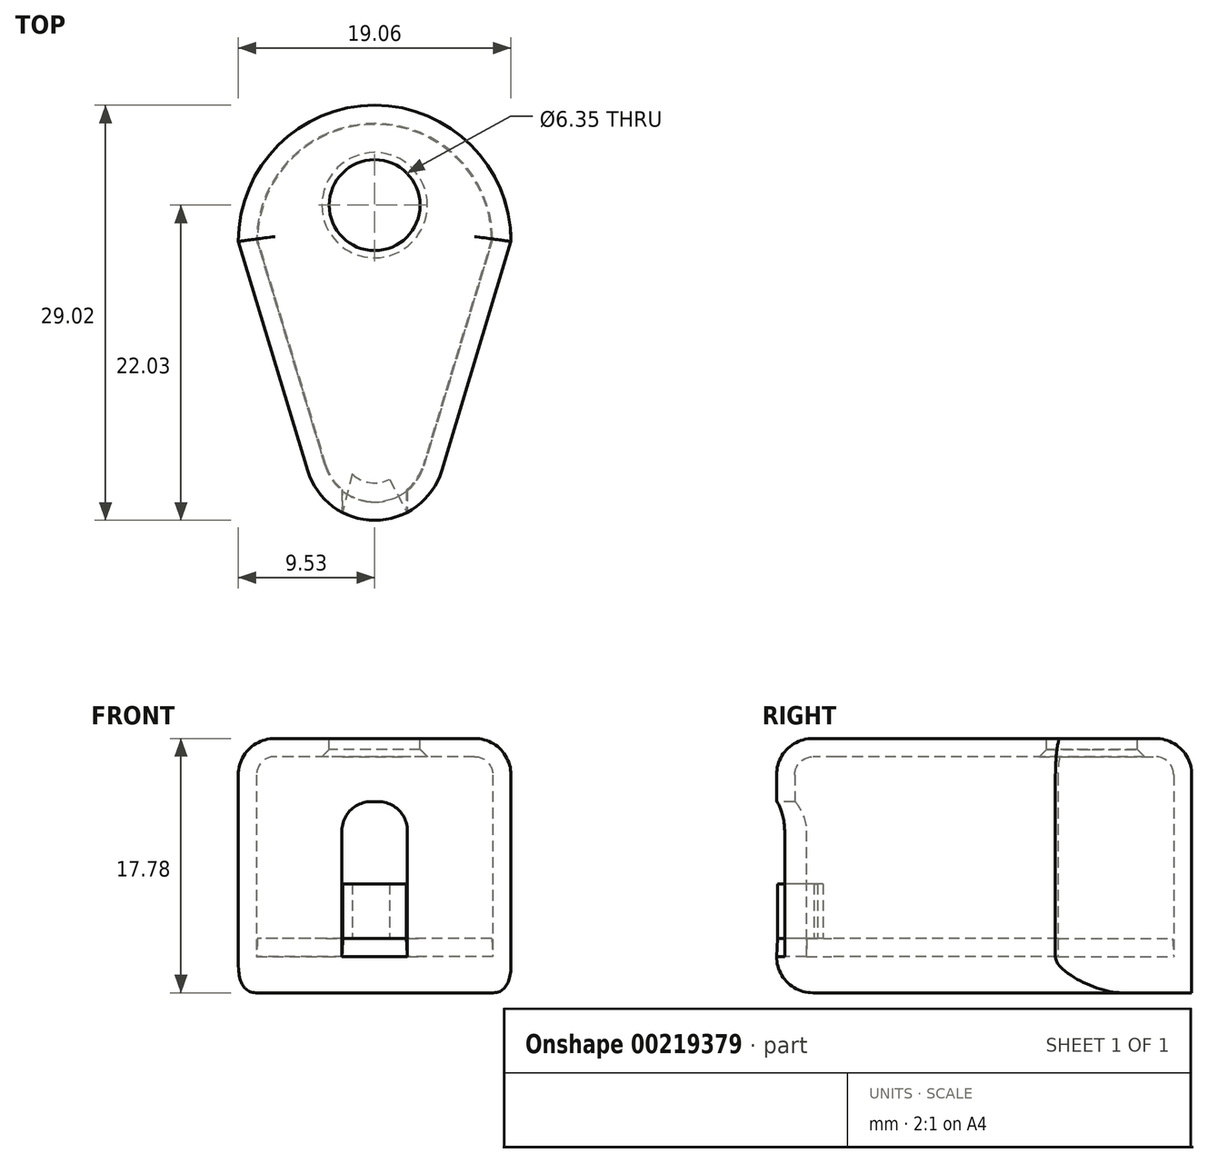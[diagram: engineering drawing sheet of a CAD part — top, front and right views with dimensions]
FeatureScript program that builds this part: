
annotation { "Feature Type Name" : "Feature", "Feature Type Description" : "" }
export const myFeature = defineFeature(function(context is Context, id is Id, definition is map)
    precondition{}
    {
        {
            var Q0;
            Q0=qCreatedBy(makeId("Top.planeOp"),FACE);
            var sketch = newSketch(context, id + "F0", { "sketchPlane" : qUnion([Q0])});
            skArc(sketch, "E0", {"start": v(9.53, 0) * mm, "mid": v(0, 9.53) * mm, "end": v(-9.53, 0) * mm});
            skLineSegment(sketch, "E1", {"start": v(-9.53, 0) * mm, "end": v(-4.68, -16.01) * mm});
            skLineSegment(sketch, "E2.MirrorCS", {"start": v(9.53, 0) * mm, "end": v(4.68, -16.01) * mm});
            skArc(sketch, "E3", {"start": v(-4.68, -16.01) * mm, "mid": v(0, -19.49) * mm, "end": v(4.68, -16.01) * mm});
            skSolve(sketch);
        }
        {
            var Q0;
            Q0 = qSketchRegion(id + "F0", true);
            extrude(context, id + "F1", {"entities" : qUnion([Q0]), "depth" : 15.24 * mm});
        }
        {
            var Q0;
            Q0=makeQuery(id+"F1.opExtrude","CAP_EDGE",EDGE,{"disambiguationData":[OSD([sQuery(id+"F0.wireOp",EDGE,"E1")])],"isStart":false});
            var Q1;
            Q1=makeQuery(id+"F1.opExtrude","CAP_EDGE",EDGE,{"disambiguationData":[OSD([sQuery(id+"F0.wireOp",EDGE,"E0")])],"isStart":false});
            fillet(context, id + "F2", {"entities" : qUnion([Q0, Q1]), "radius" : 2.54 * mm, "tangentPropagation" : true, "allowEdgeOverflow" : false});
        }
        {
            var Q0;
            Q0=makeQuery(id+"F1.opExtrude","CAP_FACE",FACE,{"disambiguationData":[OSD([sQuery(id+"F0.wireOp",EDGE,"E0"),sQuery(id+"F0.wireOp",EDGE,"E1"),sQuery(id+"F0.wireOp",EDGE,"E2.MirrorCS"),sQuery(id+"F0.wireOp",EDGE,"E3")])],"isStart":true});
            shell(context, id + "F3", {"entities" : qUnion([Q0]), "thickness" : 1.27 * mm});
        }
        {
            var Q0;
            Q0=makeQuery(id+"F1.opExtrude","CAP_FACE",FACE,{"disambiguationData":[OSD([sQuery(id+"F0.wireOp",EDGE,"E0"),sQuery(id+"F0.wireOp",EDGE,"E1"),sQuery(id+"F0.wireOp",EDGE,"E2.MirrorCS"),sQuery(id+"F0.wireOp",EDGE,"E3")])],"isStart":true});
            var sketch = newSketch(context, id + "F4", { "sketchPlane" : qUnion([Q0])});
            skLineSegment(sketch, "E4.bottom", {"start": v(2.29, 14.82) * mm, "end": v(-2.29, 14.82) * mm});
            skLineSegment(sketch, "E4.top", {"start": v(2.29, 27.3) * mm, "end": v(-2.29, 27.3) * mm});
            skLineSegment(sketch, "E4.left", {"start": v(2.29, 14.82) * mm, "end": v(2.29, 27.3) * mm});
            skLineSegment(sketch, "E4.right", {"start": v(-2.29, 14.82) * mm, "end": v(-2.29, 27.3) * mm});
            skPoint(sketch, "E4.middle", {"position": v(0, 21.05) * mm});
            skPoint(sketch, "E4.middle.positionSnap0", {"position": v(0, 19.49) * mm});
            skPoint(sketch, "E4.centerSnap0", {"position": v(0, 19.49) * mm});
            skSolve(sketch);
        }
        {
            var Q0;
            Q0 = qSketchRegion(id + "F4", true);
            extrude(context, id + "F5", {"entities" : qUnion([Q0]), "operationType" : NewBodyOperationType.REMOVE, "oppositeDirection" : true, "depth" : 10.82 * mm});
        }
        {
            var Q0;
            Q0=makeQuery(id+"F5.boolean.opBoolean","COPY",EDGE,{"derivedFrom":makeQuery(id+"F5.opExtrude","CAP_EDGE",EDGE,{"disambiguationData":[OSD([sQuery(id+"F4.wireOp",EDGE,"E4.left")])],"isStart":false})});
            var Q1;
            Q1=makeQuery(id+"F5.boolean.opBoolean","COPY",EDGE,{"derivedFrom":makeQuery(id+"F5.opExtrude","CAP_EDGE",EDGE,{"disambiguationData":[OSD([sQuery(id+"F4.wireOp",EDGE,"E4.right")])],"isStart":false})});
            fillet(context, id + "F6", {"entities" : qUnion([Q0, Q1]), "radius" : 2.03 * mm, "allowEdgeOverflow" : false});
        }
        {
            var Q0;
            Q0=makeQuery(id+"F1.opExtrude","CAP_FACE",FACE,{"disambiguationData":[OSD([sQuery(id+"F0.wireOp",EDGE,"E0"),sQuery(id+"F0.wireOp",EDGE,"E1"),sQuery(id+"F0.wireOp",EDGE,"E2.MirrorCS"),sQuery(id+"F0.wireOp",EDGE,"E3")])],"isStart":false});
            var sketch = newSketch(context, id + "F7", { "sketchPlane" : qUnion([Q0])});
            skCircle(sketch, "E5", {"center": v(0, 2.54) * mm, "radius": 3.18 * mm});
            skSolve(sketch);
        }
        {
            var Q0;
            Q0 = qSketchRegion(id + "F7", true);
            extrude(context, id + "F8", {"entities" : qUnion([Q0]), "operationType" : NewBodyOperationType.REMOVE, "endBound" : BoundingType.THROUGH_ALL, "oppositeDirection" : true, "depth" : 25.4 * mm});
        }
        {
            var Q0;
            Q0=makeQuery(id+"F1.opExtrude","CAP_FACE",FACE,{"disambiguationData":[OSD([sQuery(id+"F0.wireOp",EDGE,"E0"),sQuery(id+"F0.wireOp",EDGE,"E1"),sQuery(id+"F0.wireOp",EDGE,"E2.MirrorCS"),sQuery(id+"F0.wireOp",EDGE,"E3")])],"isStart":true});
            var sketch = newSketch(context, id + "F9", { "sketchPlane" : qUnion([Q0])});
            skLineSegment(sketch, "E6.0", {"start": v(-9.53, 0) * mm, "end": v(-4.68, 16.01) * mm});
            skArc(sketch, "E7.0", {"start": v(9.53, 0) * mm, "mid": v(0, -9.53) * mm, "end": v(-9.53, 0) * mm});
            skLineSegment(sketch, "E7.1", {"start": v(9.53, 0) * mm, "end": v(4.68, 16.01) * mm});
            skArc(sketch, "E7.2", {"start": v(4.68, 16.01) * mm, "mid": v(0, 19.49) * mm, "end": v(-4.68, 16.01) * mm});
            skSolve(sketch);
        }
        {
            var Q0;
            Q0 = qSketchRegion(id + "F9", true);
            extrude(context, id + "F10", {"entities" : qUnion([Q0]), "depth" : 2.54 * mm});
        }
        {
            var Q0;
            Q0=makeQuery(id+"F10.opExtrude","CAP_FACE",FACE,{"disambiguationData":[OSD([sQuery(id+"F9.wireOp",EDGE,"E6.0"),sQuery(id+"F9.wireOp",EDGE,"E7.0"),sQuery(id+"F9.wireOp",EDGE,"E7.1"),sQuery(id+"F9.wireOp",EDGE,"E7.2")])],"isStart":true});
            var sketch = newSketch(context, id + "F11", { "sketchPlane" : qUnion([Q0])});
            skArc(sketch, "E8.0", {"start": v(8.25, 0.18) * mm, "mid": v(0, 8.26) * mm, "end": v(-8.25, 0.18) * mm});
            skLineSegment(sketch, "E9.0", {"start": v(8.25, 0.18) * mm, "end": v(3.47, -15.64) * mm});
            skLineSegment(sketch, "E10.0", {"start": v(-8.25, 0.18) * mm, "end": v(-3.47, -15.64) * mm});
            skArc(sketch, "E11.0", {"start": v(-3.47, -15.64) * mm, "mid": v(-3, -16.61) * mm, "end": v(-2.29, -17.4) * mm});
            skArc(sketch, "E12.0", {"start": v(2.29, -17.4) * mm, "mid": v(3, -16.61) * mm, "end": v(3.47, -15.64) * mm});
            skLineSegment(sketch, "E13.0", {"start": v(2.29, -17.4) * mm, "end": v(2.29, -18.92) * mm});
            skLineSegment(sketch, "E14.0", {"start": v(-2.29, -17.4) * mm, "end": v(-2.29, -18.92) * mm});
            skArc(sketch, "E15.0", {"start": v(-2.29, -18.92) * mm, "mid": v(0, -19.49) * mm, "end": v(2.29, -18.92) * mm});
            skPoint(sketch, "E16.orphan", {"position": v(4.68, -16.01) * mm});
            skPoint(sketch, "E17.orphan", {"position": v(-4.68, -16.01) * mm});
            skSolve(sketch);
        }
        {
            var Q0;
            Q0 = qSketchRegion(id + "F11", true);
            extrude(context, id + "F12", {"entities" : qUnion([Q0]), "operationType" : NewBodyOperationType.ADD, "depth" : 1.27 * mm, "hasDraft" : true, "draftAngle" : 3 * degree, "draftPullDirection" : true});
        }
        {
            var Q0;
            Q0=makeQuery(id+"F10.opExtrude","CAP_EDGE",EDGE,{"disambiguationData":[OSD([sQuery(id+"F9.wireOp",EDGE,"E7.1")])],"isStart":false});
            fillet(context, id + "F13", {"entities" : qUnion([Q0]), "radius" : 2.54 * mm, "tangentPropagation" : true, "allowEdgeOverflow" : false});
        }
        {
            var Q0;
            Q0=makeQuery(id+"F12.opExtrude","CAP_FACE",FACE,{"disambiguationData":[OSD([sQuery(id+"F11.wireOp",EDGE,"E8.0"),sQuery(id+"F11.wireOp",EDGE,"E9.0"),sQuery(id+"F11.wireOp",EDGE,"E10.0"),sQuery(id+"F11.wireOp",EDGE,"E11.0"),sQuery(id+"F11.wireOp",EDGE,"E12.0"),sQuery(id+"F11.wireOp",EDGE,"E13.0"),sQuery(id+"F11.wireOp",EDGE,"E14.0"),sQuery(id+"F11.wireOp",EDGE,"E15.0")])],"isStart":false});
            var sketch = newSketch(context, id + "F14", { "sketchPlane" : qUnion([Q0])});
            skArc(sketch, "E18.0", {"start": v(-2.22, -18.88) * mm, "mid": v(0, -19.42) * mm, "end": v(2.22, -18.88) * mm});
            skArc(sketch, "E19.0", {"start": v(-1.57, -16.26) * mm, "mid": v(-0.32, -16.86) * mm, "end": v(1.05, -16.62) * mm});
            skLineSegment(sketch, "E20", {"start": v(1.05, -16.62) * mm, "end": v(2.22, -18.88) * mm});
            skLineSegment(sketch, "E21", {"start": v(-1.57, -16.26) * mm, "end": v(-2.22, -18.88) * mm});
            skSolve(sketch);
        }
        {
            var Q0;
            Q0 = qSketchRegion(id + "F14", true);
            extrude(context, id + "F15", {"entities" : qUnion([Q0]), "operationType" : NewBodyOperationType.ADD, "depth" : 3.8 * mm});
        }
        {
            var Q0;
            Q0=makeQuery(id+"F8.boolean.opBoolean","INTERSECT",EDGE,{"derivedFrom":[makeQuery(id+"F3.opShell","OFFSET_FACE",FACE,{"disambiguationData":[OSD([sQuery(id+"F0.wireOp",EDGE,"E0"),sQuery(id+"F0.wireOp",EDGE,"E1"),sQuery(id+"F0.wireOp",EDGE,"E2.MirrorCS"),sQuery(id+"F0.wireOp",EDGE,"E3")])]}),makeQuery(id+"F8.opExtrude","SWEPT_FACE",FACE,{"disambiguationData":[OSD([sQuery(id+"F7.wireOp",EDGE,"E5")])]})]});
            chamfer(context, id + "F16", {"entities" : qUnion([Q0]), "width" : 0.5 * mm, "tangentPropagation" : true});
        }
    });
